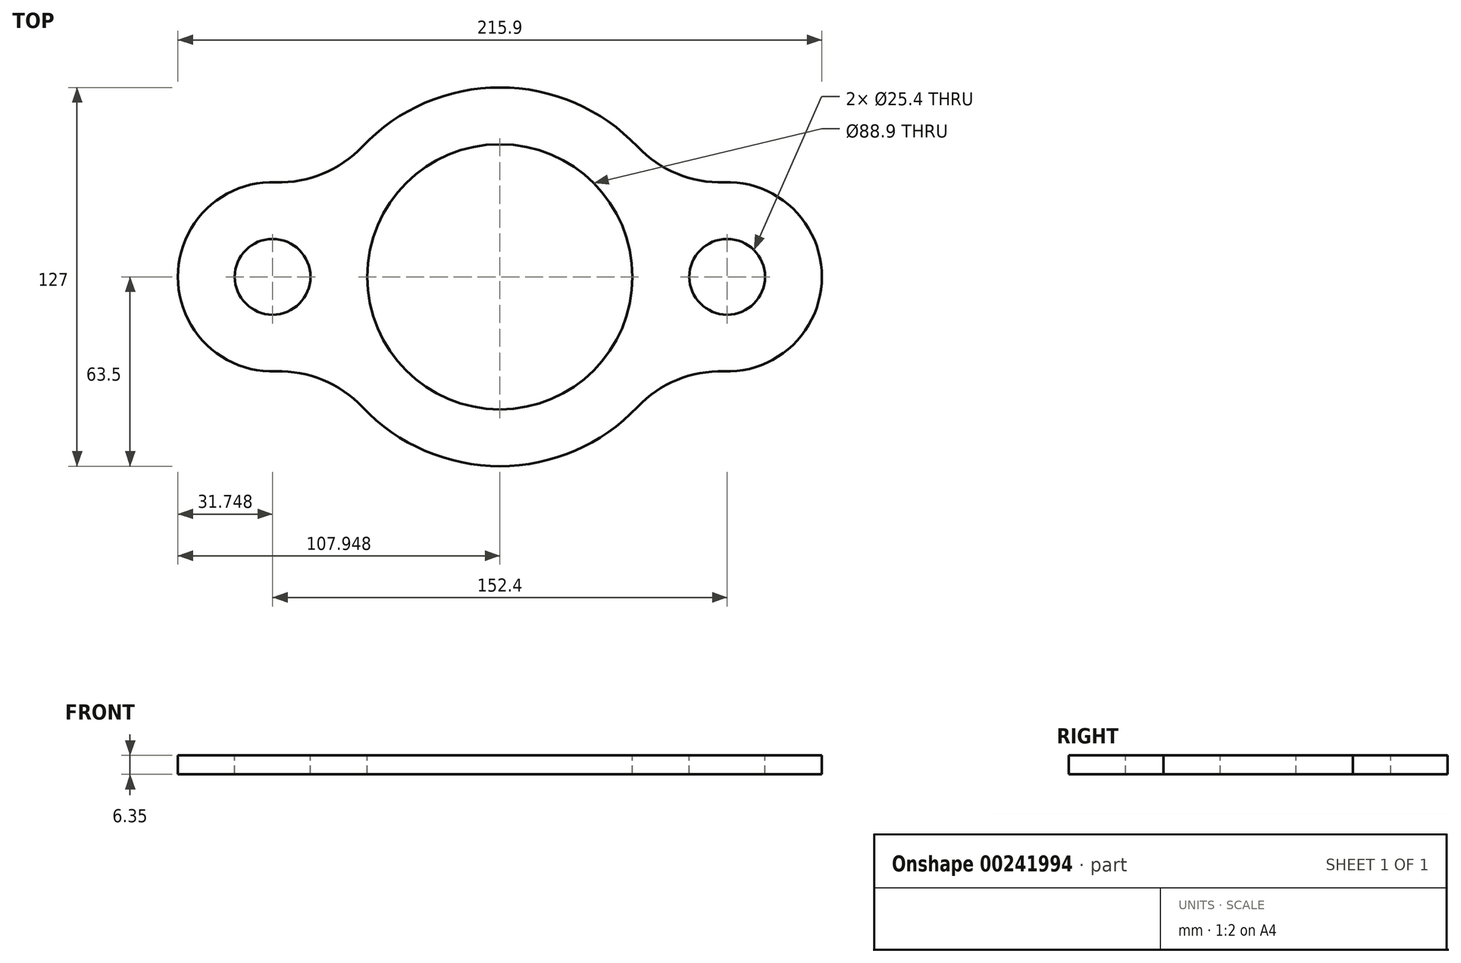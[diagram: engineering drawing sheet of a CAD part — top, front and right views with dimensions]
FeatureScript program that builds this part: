
annotation { "Feature Type Name" : "Feature", "Feature Type Description" : "" }
export const myFeature = defineFeature(function(context is Context, id is Id, definition is map)
    precondition{}
    {
        {
            var Q0;
            Q0=qCreatedBy(makeId("Top.planeOp"),FACE);
            var sketch = newSketch(context, id + "F0", { "sketchPlane" : qUnion([Q0])});
            skCircle(sketch, "E0", {"center": v(14.35, -6.8) * mm, "radius": 44.45 * mm});
            skArc(sketch, "E1", {"start": v(60.48, 36.83) * mm, "mid": v(14.35, 56.7) * mm, "end": v(-31.79, 36.83) * mm});
            skArc(sketch, "E2", {"start": v(89.47, -38.53) * mm, "mid": v(122.3, -6.8) * mm, "end": v(89.47, 24.93) * mm});
            skCircle(sketch, "E3", {"center": v(90.55, -6.8) * mm, "radius": 12.7 * mm});
            skArc(sketch, "E4", {"start": v(-60.77, 24.93) * mm, "mid": v(-93.6, -6.8) * mm, "end": v(-60.77, -38.53) * mm});
            skCircle(sketch, "E5", {"center": v(-61.85, -6.8) * mm, "radius": 12.7 * mm});
            skArc(sketch, "E6", {"start": v(-60.77, 24.93) * mm, "mid": v(-45, 27.76) * mm, "end": v(-31.79, 36.83) * mm});
            skArc(sketch, "E7", {"start": v(60.48, 36.83) * mm, "mid": v(73.7, 27.76) * mm, "end": v(89.47, 24.93) * mm});
            skArc(sketch, "E8", {"start": v(-31.79, -50.43) * mm, "mid": v(-45, -41.37) * mm, "end": v(-60.77, -38.53) * mm});
            skArc(sketch, "E9", {"start": v(89.47, -38.53) * mm, "mid": v(73.7, -41.37) * mm, "end": v(60.48, -50.43) * mm});
            skPoint(sketch, "E10.orphan", {"position": v(126.27, 63) * mm});
            skArc(sketch, "E11.trimOffspring", {"start": v(-31.79, -50.43) * mm, "mid": v(14.35, -70.3) * mm, "end": v(60.48, -50.43) * mm});
            skSolve(sketch);
        }
        {
            var Q0;
            Q0 = qSketchRegion(id + "F0", true);
            var Q1;
            Q1=sQuery(id+"F0.wireOp",EDGE,"E4");
            var Q2;
            Q2=sQuery(id+"F0.wireOp",EDGE,"E6");
            var Q3;
            Q3=sQuery(id+"F0.wireOp",EDGE,"E1");
            var Q4;
            Q4=sQuery(id+"F0.wireOp",EDGE,"E7");
            var Q5;
            Q5=sQuery(id+"F0.wireOp",EDGE,"E2");
            var Q6;
            Q6=sQuery(id+"F0.wireOp",EDGE,"E9");
            var Q7;
            Q7=sQuery(id+"F0.wireOp",EDGE,"E11.trimOffspring");
            var Q8;
            Q8=sQuery(id+"F0.wireOp",EDGE,"E8");
            var Q9;
            Q9=sQuery(id+"F0.wireOp",EDGE,"E5");
            var Q10;
            Q10=sQuery(id+"F0.wireOp",EDGE,"E0");
            var Q11;
            Q11=sQuery(id+"F0.wireOp",EDGE,"E3");
            extrude(context, id + "F1", {"entities" : qUnion([Q0]), "surfaceEntities" : qUnion([Q1, Q2, Q3, Q4, Q5, Q6, Q7, Q8, Q9, Q10, Q11]), "oppositeDirection" : true, "depth" : 6.35 * mm});
        }
    });
